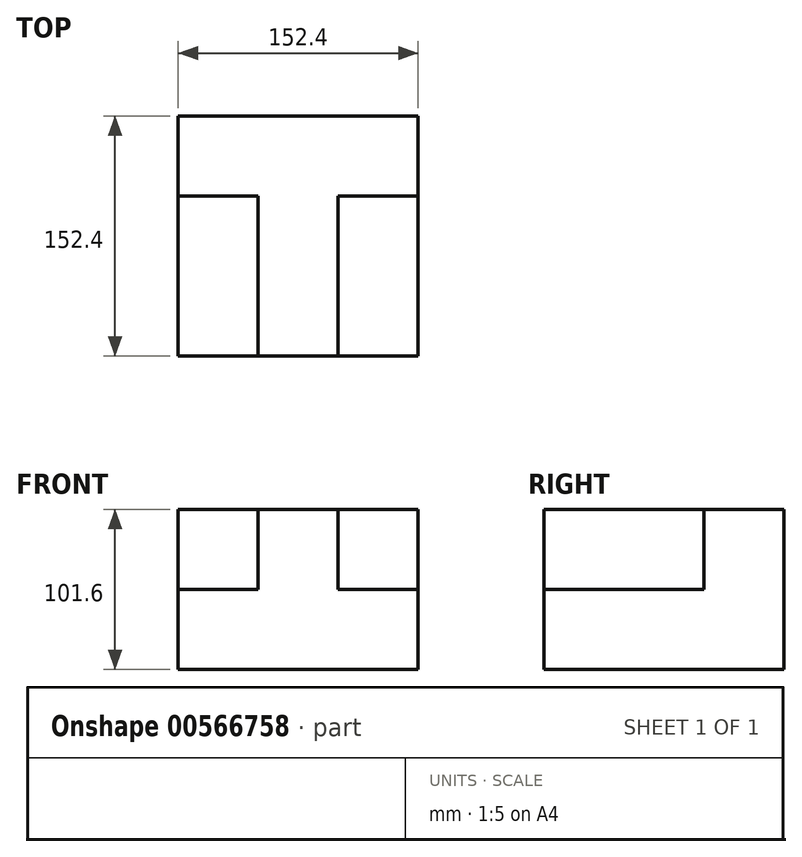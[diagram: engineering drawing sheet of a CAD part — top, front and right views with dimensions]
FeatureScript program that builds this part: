
annotation { "Feature Type Name" : "Feature", "Feature Type Description" : "" }
export const myFeature = defineFeature(function(context is Context, id is Id, definition is map)
    precondition{}
    {
        {
            var Q0;
            Q0=qCreatedBy(makeId("Top.planeOp"),FACE);
            var sketch = newSketch(context, id + "F0", { "sketchPlane" : qUnion([Q0])});
            skLineSegment(sketch, "E0.bottom", {"start": v(-106.93, -60.63) * mm, "end": v(45.47, -60.63) * mm});
            skLineSegment(sketch, "E0.top", {"start": v(-106.93, 91.77) * mm, "end": v(45.47, 91.77) * mm});
            skLineSegment(sketch, "E0.left", {"start": v(-106.93, -60.63) * mm, "end": v(-106.93, 91.77) * mm});
            skLineSegment(sketch, "E0.right", {"start": v(45.47, -60.63) * mm, "end": v(45.47, 91.77) * mm});
            skSolve(sketch);
        }
        {
            var Q0;
            Q0=makeQuery(id+"F0.imprint","IMPRINT",FACE,{"disambiguationData":[TD([[makeQuery(id+"F0.imprint","IMPRINT",EDGE,{"derivedFrom":sQuery(id+"F0.wireOp",EDGE,"E0.bottom")}),1.0]])]});
            extrude(context, id + "F1", {"entities" : qUnion([Q0]), "depth" : 101.6 * mm, "offsetDistance" : 25.4 * mm});
        }
        {
            var Q0;
            Q0=makeQuery(id+"F1.opExtrude","CAP_FACE",FACE,{"disambiguationData":[OSD([sQuery(id+"F0.wireOp",EDGE,"E0.bottom"),sQuery(id+"F0.wireOp",EDGE,"E0.top"),sQuery(id+"F0.wireOp",EDGE,"E0.left"),sQuery(id+"F0.wireOp",EDGE,"E0.right")])],"isStart":false});
            var sketch = newSketch(context, id + "F2", { "sketchPlane" : qUnion([Q0])});
            skLineSegment(sketch, "E1.bottom", {"start": v(-106.93, 91.77) * mm, "end": v(45.47, 91.77) * mm});
            skLineSegment(sketch, "E1.top", {"start": v(-106.93, 40.97) * mm, "end": v(45.47, 40.97) * mm});
            skLineSegment(sketch, "E1.left", {"start": v(-106.93, 91.77) * mm, "end": v(-106.93, 40.97) * mm});
            skLineSegment(sketch, "E1.right", {"start": v(45.47, 91.77) * mm, "end": v(45.47, 40.97) * mm});
            skLineSegment(sketch, "E2.bottom", {"start": v(45.47, -60.63) * mm, "end": v(-5.33, -60.63) * mm});
            skLineSegment(sketch, "E2.top", {"start": v(45.47, 40.97) * mm, "end": v(-5.33, 40.97) * mm});
            skLineSegment(sketch, "E2.left", {"start": v(45.47, -60.63) * mm, "end": v(45.47, 40.97) * mm});
            skLineSegment(sketch, "E2.right", {"start": v(-5.33, -60.63) * mm, "end": v(-5.33, 40.97) * mm});
            skLineSegment(sketch, "E3.bottom", {"start": v(-106.93, -60.63) * mm, "end": v(-56.13, -60.63) * mm});
            skLineSegment(sketch, "E3.top", {"start": v(-106.93, 40.97) * mm, "end": v(-56.13, 40.97) * mm});
            skLineSegment(sketch, "E3.left", {"start": v(-106.93, -60.63) * mm, "end": v(-106.93, 40.97) * mm});
            skLineSegment(sketch, "E3.right", {"start": v(-56.13, -60.63) * mm, "end": v(-56.13, 40.97) * mm});
            skSolve(sketch);
        }
        {
            var Q0;
            Q0=makeQuery(id+"F2.imprint","IMPRINT",FACE,{"disambiguationData":[TD([[makeQuery(id+"F2.imprint","IMPRINT",EDGE,{"derivedFrom":sQuery(id+"F2.wireOp",EDGE,"E2.bottom")}),1.0]])]});
            var Q1;
            Q1=makeQuery(id+"F2.imprint","IMPRINT",FACE,{"disambiguationData":[TD([[makeQuery(id+"F2.imprint","IMPRINT",EDGE,{"derivedFrom":sQuery(id+"F2.wireOp",EDGE,"E3.bottom")}),1.0]])]});
            extrude(context, id + "F3", {"entities" : qUnion([Q0, Q1]), "operationType" : NewBodyOperationType.REMOVE, "oppositeDirection" : true, "depth" : 50.8 * mm, "offsetDistance" : 25.4 * mm});
        }
    });
